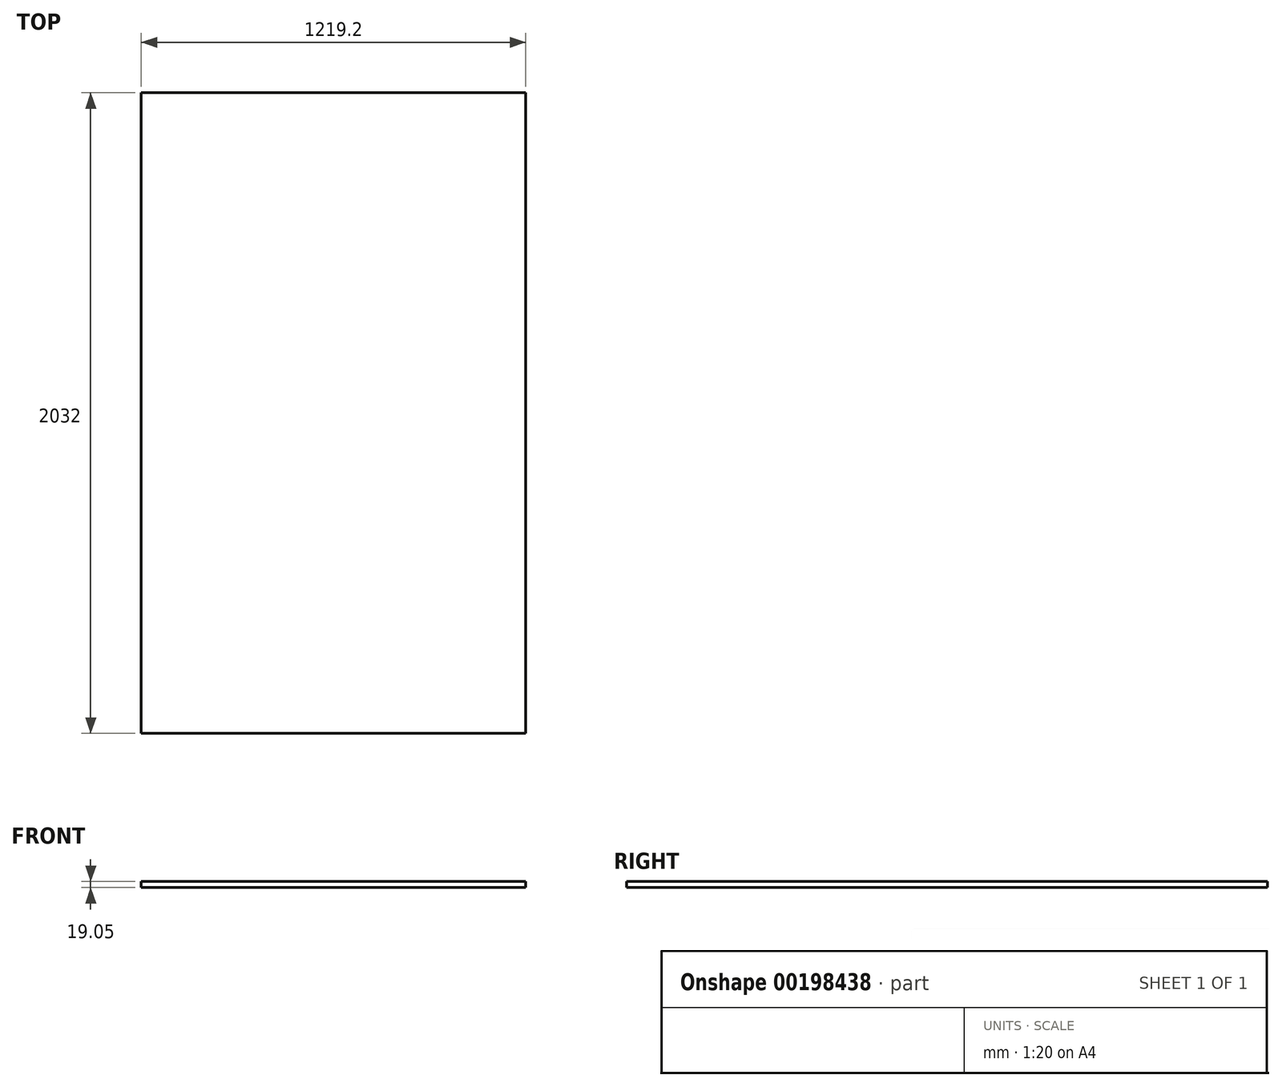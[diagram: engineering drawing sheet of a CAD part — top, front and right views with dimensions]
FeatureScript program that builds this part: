
annotation { "Feature Type Name" : "Feature", "Feature Type Description" : "" }
export const myFeature = defineFeature(function(context is Context, id is Id, definition is map)
    precondition{}
    {
        {
            var Q0;
            Q0=qCreatedBy(makeId("Top.planeOp"),FACE);
            var sketch = newSketch(context, id + "F0", { "sketchPlane" : qUnion([Q0])});
            skLineSegment(sketch, "E0.bottom", {"start": v(-609.6, 1016) * mm, "end": v(609.6, 1016) * mm});
            skLineSegment(sketch, "E0.top", {"start": v(-609.6, -1016) * mm, "end": v(609.6, -1016) * mm});
            skLineSegment(sketch, "E0.left", {"start": v(-609.6, 1016) * mm, "end": v(-609.6, -1016) * mm});
            skLineSegment(sketch, "E0.right", {"start": v(609.6, 1016) * mm, "end": v(609.6, -1016) * mm});
            skPoint(sketch, "E0.middle", {"position": v(0, 0) * mm});
            skSolve(sketch);
        }
        {
            var Q0;
            Q0=makeQuery(id+"F0.imprint","IMPRINT",FACE,{"disambiguationData":[TD([[makeQuery(id+"F0.imprint","IMPRINT",EDGE,{"derivedFrom":sQuery(id+"F0.wireOp",EDGE,"E0.bottom")}),-1.0]])]});
            extrude(context, id + "F1", {"entities" : qUnion([Q0]), "depth" : 19.05 * mm});
        }
    });
